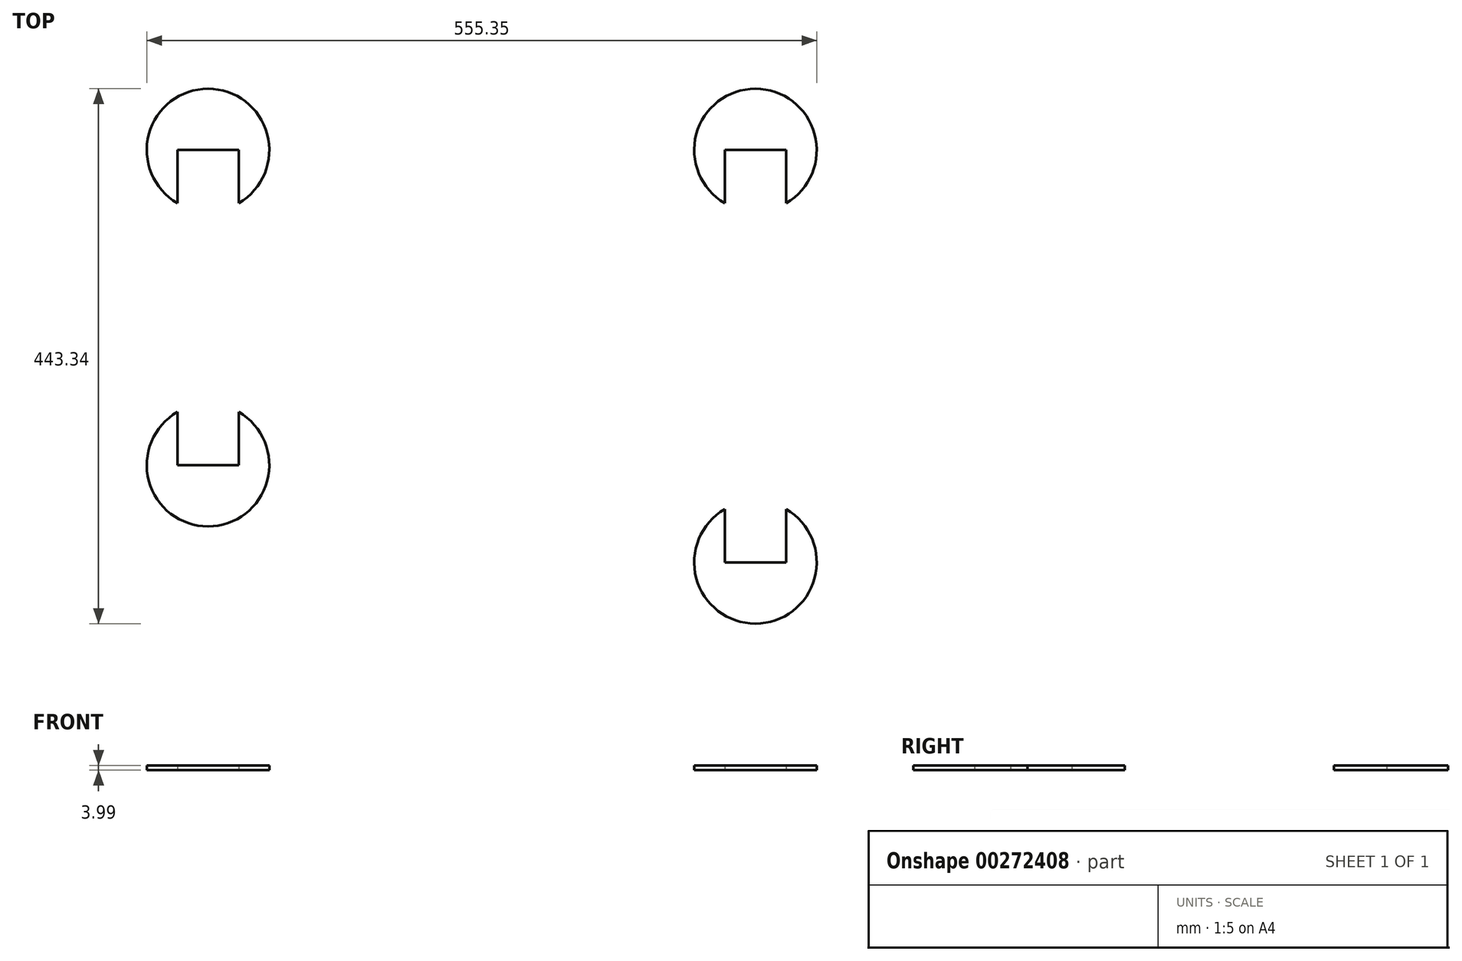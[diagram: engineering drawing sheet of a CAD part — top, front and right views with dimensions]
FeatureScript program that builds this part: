
annotation { "Feature Type Name" : "Feature", "Feature Type Description" : "" }
export const myFeature = defineFeature(function(context is Context, id is Id, definition is map)
    precondition{}
    {
        {
            var Q0;
            Q0=qCreatedBy(makeId("Top.planeOp"),FACE);
            var sketch = newSketch(context, id + "F0", { "sketchPlane" : qUnion([Q0])});
            skArc(sketch, "E0", {"start": v(-138.72, -14.14) * mm, "mid": v(-164.12, 80.65) * mm, "end": v(-189.52, -14.14) * mm});
            skLineSegment(sketch, "E1", {"start": v(-164.12, 29.85) * mm, "end": v(-214.92, 29.85) * mm});
            skLineSegment(sketch, "E2", {"start": v(-164.12, 29.85) * mm, "end": v(-113.32, 29.85) * mm});
            skLineSegment(sketch, "E3", {"start": v(-189.52, 29.85) * mm, "end": v(-189.52, -14.14) * mm});
            skLineSegment(sketch, "E4", {"start": v(-138.72, 29.85) * mm, "end": v(-138.72, -14.14) * mm});
            skLineSegment(sketch, "E5", {"start": v(62.76, -16.22) * mm, "end": v(62.76, -67.01) * mm});
            skArc(sketch, "E6.MirrorCS", {"start": v(264.23, -14.14) * mm, "mid": v(289.63, 80.65) * mm, "end": v(315.03, -14.14) * mm});
            skLineSegment(sketch, "E7.MirrorCS", {"start": v(289.63, 29.85) * mm, "end": v(238.83, 29.85) * mm});
            skLineSegment(sketch, "E8.MirrorCS", {"start": v(289.63, 29.85) * mm, "end": v(340.43, 29.85) * mm});
            skLineSegment(sketch, "E9.MirrorCS", {"start": v(315.03, 29.85) * mm, "end": v(315.03, -14.14) * mm});
            skLineSegment(sketch, "E10.MirrorCS", {"start": v(264.23, 29.85) * mm, "end": v(264.23, -14.14) * mm});
            skLineSegment(sketch, "E11", {"start": v(-6.71, 47.78) * mm, "end": v(-6.71, -8.2) * mm});
            skLineSegment(sketch, "E12", {"start": v(20.52, 47.54) * mm, "end": v(20.52, -13.99) * mm});
            skLineSegment(sketch, "E13", {"start": v(-53.88, -100.71) * mm, "end": v(-36.3, -100.71) * mm, "construction": true});
            skLineSegment(sketch, "E14.MirrorCS", {"start": v(-164.12, -231.28) * mm, "end": v(-214.92, -231.28) * mm});
            skLineSegment(sketch, "E15.MirrorCS", {"start": v(-189.52, -231.28) * mm, "end": v(-189.52, -187.29) * mm});
            skLineSegment(sketch, "E16.MirrorCS", {"start": v(-164.12, -231.28) * mm, "end": v(-113.32, -231.28) * mm});
            skArc(sketch, "E17.MirrorCS", {"start": v(-138.72, -187.29) * mm, "mid": v(-164.12, -282.08) * mm, "end": v(-189.52, -187.29) * mm});
            skLineSegment(sketch, "E18.MirrorCS", {"start": v(-138.72, -231.28) * mm, "end": v(-138.72, -187.29) * mm});
            skLineSegment(sketch, "E19", {"start": v(-139.85, -141.02) * mm, "end": v(-125.28, -141.02) * mm, "construction": true});
            skLineSegment(sketch, "E20.MirrorCS", {"start": v(289.63, -311.9) * mm, "end": v(238.83, -311.9) * mm});
            skArc(sketch, "E21.MirrorCS", {"start": v(264.23, -267.9) * mm, "mid": v(289.63, -362.7) * mm, "end": v(315.03, -267.9) * mm});
            skLineSegment(sketch, "E22.MirrorCS", {"start": v(289.63, -311.9) * mm, "end": v(340.43, -311.9) * mm});
            skLineSegment(sketch, "E23.MirrorCS", {"start": v(264.23, -311.9) * mm, "end": v(264.23, -267.9) * mm});
            skLineSegment(sketch, "E24.MirrorCS", {"start": v(315.03, -311.9) * mm, "end": v(315.03, -267.9) * mm});
            skSolve(sketch);
        }
        {
            var Q0;
            Q0 = qSketchRegion(id + "F0", true);
            extrude(context, id + "F1", {"entities" : qUnion([Q0]), "depth" : 4 * mm});
        }
    });
